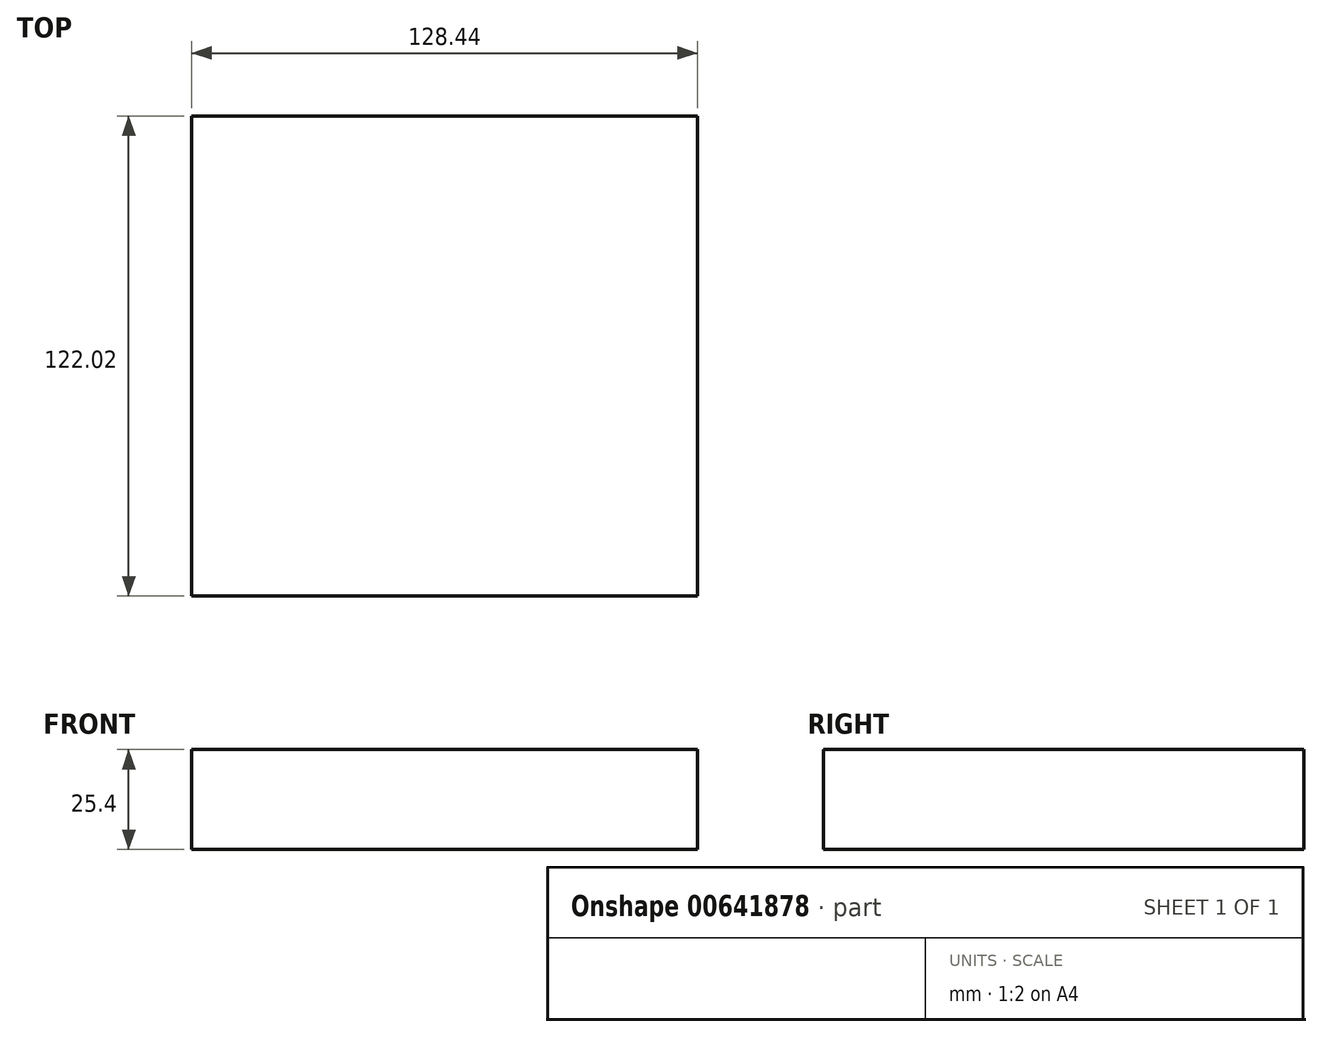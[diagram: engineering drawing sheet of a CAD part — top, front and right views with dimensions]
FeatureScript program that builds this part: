
annotation { "Feature Type Name" : "Feature", "Feature Type Description" : "" }
export const myFeature = defineFeature(function(context is Context, id is Id, definition is map)
    precondition{}
    {
        {
            var Q0;
            Q0=qCreatedBy(makeId("Top.planeOp"),FACE);
            var sketch = newSketch(context, id + "F0", { "sketchPlane" : qUnion([Q0])});
            skLineSegment(sketch, "E0.bottom", {"start": v(-65.15, -58.6) * mm, "end": v(63.29, -58.6) * mm});
            skLineSegment(sketch, "E0.top", {"start": v(-65.15, 63.42) * mm, "end": v(63.29, 63.42) * mm});
            skLineSegment(sketch, "E0.left", {"start": v(-65.15, -58.6) * mm, "end": v(-65.15, 63.42) * mm});
            skLineSegment(sketch, "E0.right", {"start": v(63.29, -58.6) * mm, "end": v(63.29, 63.42) * mm});
            skSolve(sketch);
        }
        {
            var Q0;
            Q0 = qSketchRegion(id + "F0", true);
            extrude(context, id + "F1", {"entities" : qUnion([Q0]), "depth" : 25.4 * mm, "offsetDistance" : 25.4 * mm});
        }
        {
            var Q0;
            Q0=qCreatedBy(makeId("Front.planeOp"),FACE);
            var sketch = newSketch(context, id + "F2", { "sketchPlane" : qUnion([Q0])});
            skCircle(sketch, "E1.cCircle", {"center": v(-2.75, 25.44) * mm, "radius": 20.74 * mm, "construction": true});
            skLineSegment(sketch, "E1.0", {"start": v(18, 40.5) * mm, "end": v(18, 10.37) * mm});
            skLineSegment(sketch, "E1.1", {"start": v(18, 10.37) * mm, "end": v(-10.67, 1.05) * mm});
            skLineSegment(sketch, "E1.2", {"start": v(-10.67, 1.05) * mm, "end": v(-28.39, 25.44) * mm});
            skLineSegment(sketch, "E1.3", {"start": v(-28.39, 25.44) * mm, "end": v(-10.67, 49.82) * mm});
            skLineSegment(sketch, "E1.4", {"start": v(-10.67, 49.82) * mm, "end": v(18, 40.5) * mm});
            skPoint(sketch, "E1.0.midPoint", {"position": v(18, 25.44) * mm});
            skSolve(sketch);
        }
        {
            var Q0;
            Q0=sQuery(id+"F2.wireOp",EDGE,"E1.1");
            var Q1;
            Q1=sQuery(id+"F2.wireOp",EDGE,"E1.2");
            var Q2;
            Q2=sQuery(id+"F2.wireOp",EDGE,"E1.0");
            var Q3;
            Q3=sQuery(id+"F2.wireOp",EDGE,"E1.4");
            var Q4;
            Q4=sQuery(id+"F2.wireOp",EDGE,"E1.3");
            extrude(context, id + "F3", {"bodyType" : ToolBodyType.SURFACE, "surfaceEntities" : qUnion([Q0, Q1, Q2, Q3, Q4]), "depth" : 50.8 * mm, "offsetDistance" : 25.4 * mm});
        }
    });
